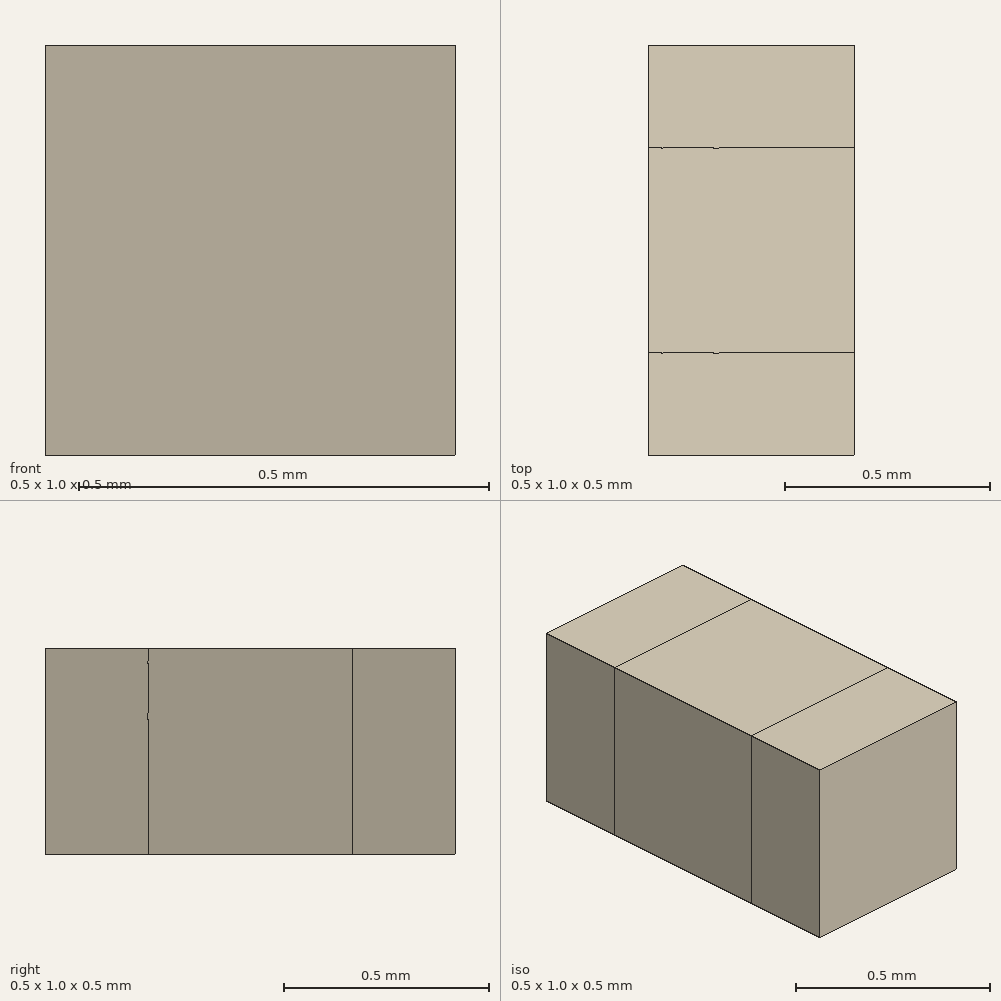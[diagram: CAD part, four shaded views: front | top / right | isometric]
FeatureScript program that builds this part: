
annotation { "Feature Type Name" : "Feature", "Feature Type Description" : "" }
export const myFeature = defineFeature(function(context is Context, id is Id, definition is map)
    precondition{}
    {
        {
            var Q0;
            Q0=qCreatedBy(makeId("Top.planeOp"),FACE);
            var sketch = newSketch(context, id + "F0", { "sketchPlane" : qUnion([Q0])});
            skLineSegment(sketch, "E0.bottom", {"start": v(-0.25, 0.5) * mm, "end": v(0.25, 0.5) * mm});
            skLineSegment(sketch, "E0.top", {"start": v(-0.25, -0.5) * mm, "end": v(0.25, -0.5) * mm});
            skLineSegment(sketch, "E0.left", {"start": v(-0.25, 0.5) * mm, "end": v(-0.25, -0.5) * mm});
            skLineSegment(sketch, "E0.right", {"start": v(0.25, 0.5) * mm, "end": v(0.25, -0.5) * mm});
            skPoint(sketch, "E0.middle", {"position": v(0, 0) * mm});
            skLineSegment(sketch, "E1", {"start": v(-0.25, -0.25) * mm, "end": v(0.25, -0.25) * mm});
            skLineSegment(sketch, "E2", {"start": v(-0.25, 0.25) * mm, "end": v(0.25, 0.25) * mm});
            skSolve(sketch);
        }
        {
            var Q0;
            {var subQ0=sQuery(id+"F0.wireOp",EDGE,"E0.bottom");Q0=makeQuery(id+"F0.imprint","IMPRINT",FACE,{"disambiguationData":[TD([[makeQuery(id+"F0.imprint","IMPRINT",EDGE,{"derivedFrom":subQ0}),-1.0]])]});}
            extrude(context, id + "F1", {"entities" : qUnion([Q0]), "depth" : 0.5 * mm});
        }
        {
            var Q0;
            {var subQ0=sQuery(id+"F0.wireOp",EDGE,"E0.top");Q0=makeQuery(id+"F0.imprint","IMPRINT",FACE,{"disambiguationData":[TD([[makeQuery(id+"F0.imprint","IMPRINT",EDGE,{"derivedFrom":subQ0}),1.0]])]});}
            extrude(context, id + "F2", {"entities" : qUnion([Q0]), "depth" : 0.5 * mm});
        }
        {
            var Q0;
            {var subQ0=sQuery(id+"F0.wireOp",EDGE,"E1");Q0=makeQuery(id+"F0.imprint","IMPRINT",FACE,{"disambiguationData":[TD([[makeQuery(id+"F0.imprint","IMPRINT",EDGE,{"derivedFrom":subQ0}),1.0]])]});}
            extrude(context, id + "F3", {"entities" : qUnion([Q0]), "depth" : 0.5 * mm});
        }
    });
